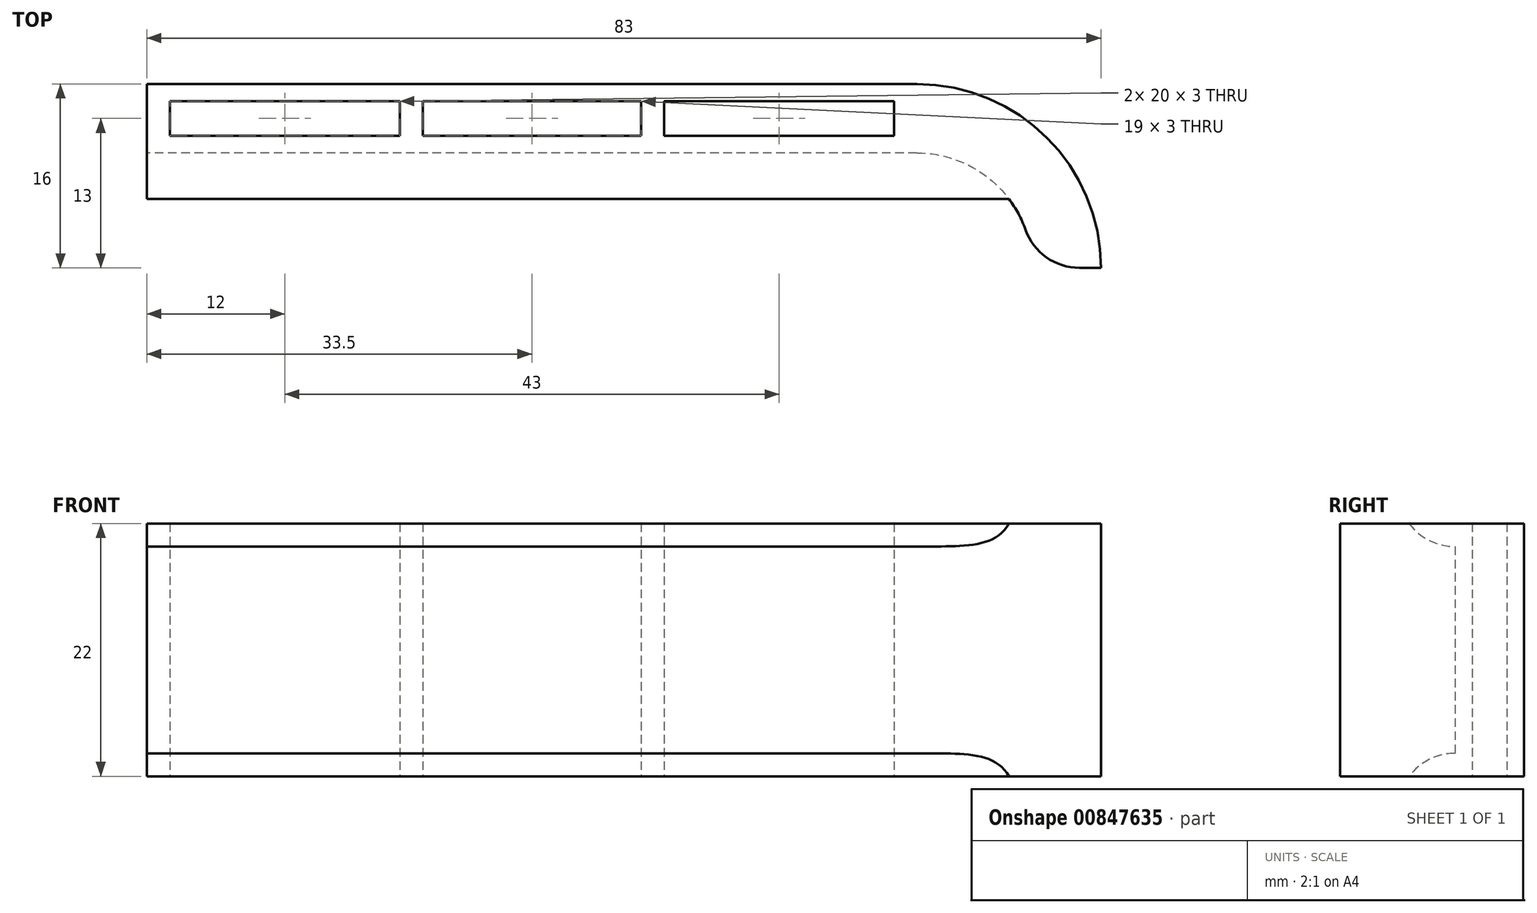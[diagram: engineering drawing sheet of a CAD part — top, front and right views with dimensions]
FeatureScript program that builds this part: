
annotation { "Feature Type Name" : "Feature", "Feature Type Description" : "" }
export const myFeature = defineFeature(function(context is Context, id is Id, definition is map)
    precondition{}
    {
        {
            var Q0;
            Q0=qCreatedBy(makeId("Top.planeOp"),FACE);
            var sketch = newSketch(context, id + "F0", { "sketchPlane" : qUnion([Q0])});
            skLineSegment(sketch, "E0.right", {"start": v(33.46, -3) * mm, "end": v(33.46, 3) * mm});
            skLineSegment(sketch, "E1.bottom", {"start": v(-33.5, 23) * mm, "end": v(33.5, 23) * mm});
            skLineSegment(sketch, "E1.top", {"start": v(-33.5, 29) * mm, "end": v(33.5, 29) * mm});
            skLineSegment(sketch, "E1.left", {"start": v(-33.5, 23) * mm, "end": v(-33.5, 29) * mm});
            skLineSegment(sketch, "E1.right", {"start": v(33.5, 23) * mm, "end": v(33.5, 29) * mm});
            skPoint(sketch, "E1.middle", {"position": v(0, 26) * mm});
            skArc(sketch, "E2", {"start": v(33.5, 29) * mm, "mid": v(49.5, 12.98) * mm, "end": v(33.46, -3) * mm});
            skArc(sketch, "E3", {"start": v(33.5, 23) * mm, "mid": v(43.5, 12.98) * mm, "end": v(33.46, 3) * mm});
            skArc(sketch, "E4", {"start": v(33.46, 3) * mm, "mid": v(40.55, 5.9) * mm, "end": v(43.5, 12.98) * mm});
            skLineSegment(sketch, "E5.bottom", {"start": v(-10.15, 23) * mm, "end": v(9.74, 23) * mm});
            skLineSegment(sketch, "E5.top", {"start": v(-9.74, 29) * mm, "end": v(10.15, 29) * mm});
            skPoint(sketch, "E6.middle", {"position": v(0, 0) * mm});
            skLineSegment(sketch, "E7.bottom", {"start": v(19.16, 23) * mm, "end": v(29.1, 23) * mm});
            skLineSegment(sketch, "E7.top", {"start": v(13.9, 29) * mm, "end": v(23.84, 29) * mm});
            skPoint(sketch, "E7.middle", {"position": v(21.5, 26) * mm});
            skPoint(sketch, "E8.middle", {"position": v(25, 0) * mm});
            skPoint(sketch, "E9.middle", {"position": v(-23, 0) * mm});
            skLineSegment(sketch, "E10.bottom", {"start": v(-29.48, 23) * mm, "end": v(-15.21, 23) * mm});
            skLineSegment(sketch, "E10.top", {"start": v(-27.79, 29) * mm, "end": v(-13.52, 29) * mm});
            skPoint(sketch, "E10.middle", {"position": v(-21.5, 26) * mm});
            skLineSegment(sketch, "E11.bottom", {"start": v(-31.5, 24.5) * mm, "end": v(-11.5, 24.5) * mm});
            skLineSegment(sketch, "E11.top", {"start": v(-31.5, 27.5) * mm, "end": v(-11.5, 27.5) * mm});
            skLineSegment(sketch, "E11.left", {"start": v(-31.5, 24.5) * mm, "end": v(-31.5, 27.5) * mm});
            skLineSegment(sketch, "E11.right", {"start": v(-11.5, 24.5) * mm, "end": v(-11.5, 27.5) * mm});
            skLineSegment(sketch, "E12.bottom", {"start": v(-9.5, 24.5) * mm, "end": v(9.5, 24.5) * mm});
            skLineSegment(sketch, "E12.top", {"start": v(-9.5, 27.5) * mm, "end": v(9.5, 27.5) * mm});
            skLineSegment(sketch, "E12.left", {"start": v(-9.5, 24.5) * mm, "end": v(-9.5, 27.5) * mm});
            skLineSegment(sketch, "E12.right", {"start": v(9.5, 24.5) * mm, "end": v(9.5, 27.5) * mm});
            skLineSegment(sketch, "E13.bottom", {"start": v(11.5, 24.5) * mm, "end": v(31.5, 24.5) * mm});
            skLineSegment(sketch, "E13.top", {"start": v(11.5, 27.5) * mm, "end": v(31.5, 27.5) * mm});
            skLineSegment(sketch, "E13.left", {"start": v(11.5, 24.5) * mm, "end": v(11.5, 27.5) * mm});
            skLineSegment(sketch, "E13.right", {"start": v(31.5, 24.5) * mm, "end": v(31.5, 27.5) * mm});
            skLineSegment(sketch, "E14.bottom", {"start": v(33.5, 13) * mm, "end": v(53.94, 13) * mm});
            skLineSegment(sketch, "E14.top", {"start": v(33.5, -4.94) * mm, "end": v(53.94, -4.94) * mm});
            skLineSegment(sketch, "E14.left", {"start": v(33.5, 13) * mm, "end": v(33.5, -4.94) * mm});
            skLineSegment(sketch, "E14.right", {"start": v(53.94, 13) * mm, "end": v(53.94, -4.94) * mm});
            skSolve(sketch);
        }
        {
            var Q0;
            {var subQ0=sQuery(id+"F0.wireOp",EDGE,"E1.right");Q0=makeQuery(id+"F0.imprint","IMPRINT",FACE,{"disambiguationData":[TD([[makeQuery(id+"F0.imprint","IMPRINT",EDGE,{"derivedFrom":subQ0}),-1.0]])]});}
            var Q1;
            {var subQ8=sQuery(id+"F0.wireOp",EDGE,"E1.left");Q1=makeQuery(id+"F0.imprint","IMPRINT",FACE,{"disambiguationData":[TD([[makeQuery(id+"F0.imprint","IMPRINT",EDGE,{"derivedFrom":subQ8}),-1.0]])]});}
            extrude(context, id + "F1", {"entities" : qUnion([Q0, Q1]), "depth" : 22 * mm, "offsetDistance" : 25 * mm});
        }
        {
            var Q0;
            Q0=makeQuery(id+"F1.opExtrude","SWEPT_FACE",FACE,{"disambiguationData":[OSD([sQuery(id+"F0.wireOp",EDGE,"E1.bottom"),sQuery(id+"F0.wireOp",EDGE,"E5.bottom"),sQuery(id+"F0.wireOp",EDGE,"E7.bottom"),sQuery(id+"F0.wireOp",EDGE,"E10.bottom")])]});
            var sketch = newSketch(context, id + "F2", { "sketchPlane" : qUnion([Q0])});
            skLineSegment(sketch, "E15.bottom", {"start": v(33.5, 22) * mm, "end": v(-33.5, 22) * mm});
            skLineSegment(sketch, "E15.top", {"start": v(33.5, 20) * mm, "end": v(-33.5, 20) * mm});
            skLineSegment(sketch, "E15.left", {"start": v(33.5, 22) * mm, "end": v(33.5, 20) * mm});
            skLineSegment(sketch, "E15.right", {"start": v(-33.5, 22) * mm, "end": v(-33.5, 20) * mm});
            skLineSegment(sketch, "E16.bottom", {"start": v(33.5, 0) * mm, "end": v(-33.5, 0) * mm});
            skLineSegment(sketch, "E16.top", {"start": v(33.5, 2) * mm, "end": v(-33.5, 2) * mm});
            skLineSegment(sketch, "E16.left", {"start": v(33.5, 0) * mm, "end": v(33.5, 2) * mm});
            skLineSegment(sketch, "E16.right", {"start": v(-33.5, 0) * mm, "end": v(-33.5, 2) * mm});
            skLineSegment(sketch, "E17.bottom", {"start": v(33.5, 2) * mm, "end": v(43.5, 2) * mm});
            skLineSegment(sketch, "E17.top", {"start": v(33.5, 0) * mm, "end": v(43.5, 0) * mm});
            skLineSegment(sketch, "E17.left", {"start": v(33.5, 2) * mm, "end": v(33.5, 0) * mm});
            skLineSegment(sketch, "E17.right", {"start": v(43.5, 2) * mm, "end": v(43.5, 0) * mm});
            skLineSegment(sketch, "E18.bottom", {"start": v(33.5, 20) * mm, "end": v(43.5, 20) * mm});
            skLineSegment(sketch, "E18.top", {"start": v(33.5, 22) * mm, "end": v(43.5, 22) * mm});
            skLineSegment(sketch, "E18.left", {"start": v(33.5, 20) * mm, "end": v(33.5, 22) * mm});
            skLineSegment(sketch, "E18.right", {"start": v(43.5, 20) * mm, "end": v(43.5, 22) * mm});
            skSolve(sketch);
        }
        {
            var Q0;
            Q0=makeQuery(id+"F2.imprint","IMPRINT",FACE,{"disambiguationData":[TD([[makeQuery(id+"F2.imprint","IMPRINT",EDGE,{"derivedFrom":sQuery(id+"F2.wireOp",EDGE,"E15.bottom")}),-1.0]])]});
            var Q1;
            Q1=makeQuery(id+"F2.imprint","IMPRINT",FACE,{"disambiguationData":[TD([[makeQuery(id+"F2.imprint","IMPRINT",EDGE,{"derivedFrom":sQuery(id+"F2.wireOp",EDGE,"E16.bottom")}),1.0]])]});
            var Q2;
            Q2=makeQuery(id+"F2.imprint","IMPRINT",FACE,{"disambiguationData":[TD([[makeQuery(id+"F2.imprint","IMPRINT",EDGE,{"derivedFrom":sQuery(id+"F2.wireOp",EDGE,"E17.bottom")}),-1.0]])]});
            var Q3;
            Q3=makeQuery(id+"F2.imprint","IMPRINT",FACE,{"disambiguationData":[TD([[makeQuery(id+"F2.imprint","IMPRINT",EDGE,{"derivedFrom":sQuery(id+"F2.wireOp",EDGE,"E18.bottom")}),1.0]])]});
            extrude(context, id + "F3", {"entities" : qUnion([Q0, Q1, Q2, Q3]), "operationType" : NewBodyOperationType.ADD, "depth" : 4 * mm, "offsetDistance" : 25 * mm});
        }
        {
            var Q0;
            Q0=makeQuery(id+"F1.opExtrude","SWEPT_EDGE",EDGE,{"disambiguationData":[OSD([sQuery(id+"F0.wireOp",EDGE,"E3"),sQuery(id+"F0.wireOp",EDGE,"E14.bottom")])]});
            fillet(context, id + "F4", {"entities" : qUnion([Q0]), "radius" : 5 * mm, "tangentPropagation" : true, "allowEdgeOverflow" : false});
        }
        {
            var Q0;
            Q0=makeQuery(id+"F3.opExtrude","CAP_EDGE",EDGE,{"disambiguationData":[OSD([sQuery(id+"F2.wireOp",EDGE,"E15.top"),sQuery(id+"F2.wireOp",EDGE,"E18.bottom")])],"isStart":false});
            var Q1;
            Q1=makeQuery(id+"F3.opExtrude","CAP_EDGE",EDGE,{"disambiguationData":[OSD([sQuery(id+"F2.wireOp",EDGE,"E16.top"),sQuery(id+"F2.wireOp",EDGE,"E17.bottom")])],"isStart":false});
            fillet(context, id + "F5", {"entities" : qUnion([Q0, Q1]), "radius" : 5 * mm, "tangentPropagation" : true, "allowEdgeOverflow" : false});
        }
    });
